# Revit family: IEK_РозеткаТелевизионная_Встраиваемая_Одноместная_ВЕГА
name_source: partatom
category: Устройства связи
units: mm (PartAtom-declared; Revit-internal decimal feet)

## family parameters
Всегда вертикально = Да
На основе рабочей плоскости = Нет
Общий = Нет
При загрузке вырезать с полостями = Нет
Размер круглого соединителя = Использовать диаметр
Сохранять ориентацию аннотаций = Да
Тип детали = Нормальный
Точка расчета площади = Нет

## types (1)
- РТВ10-ВБ
    ADSK_URL страницы изделия = https://www.iek.ru
    ADSK_Версия Revit = 2019
    ADSK_Версия семейства = 1.00
    ADSK_Единица измерения = шт
    ADSK_Завод-изготовитель = IEK
    ADSK_Код изделия = EAV10-K01-DM
    ADSK_Марка = ВЕГА
    ADSK_Масса = 0.054
    ADSK_Материал = Цвет белый
    ADSK_Материал наименование = АБС-пластик
    ADSK_Наименование = Розетка 1-местная телевизионная РТВ10-ВБ ВЕГА белый IEK
    IEK_URL = https://www.iek.ru
    IEK_Описание = Электроустановочные изделия серии "ВЕГА" IEK включают в себя розетки и выключатели для скрытого монтажа, которые хорошо впишутся в любой интерьер квартир, загородных домов, офисных и производственных помещений.
    IEK_Цена за единицу = 117.68
    KSI_CMa_Строительные материалы = 01.7.14.03
    Высота = 81 мм
    Глубина = 33 мм
    Изготовитель = IEK
    Тип монтажа = Встраиваемый
    Тип соединителя или разъема = TV-SAT
    Ширина = 82 мм
